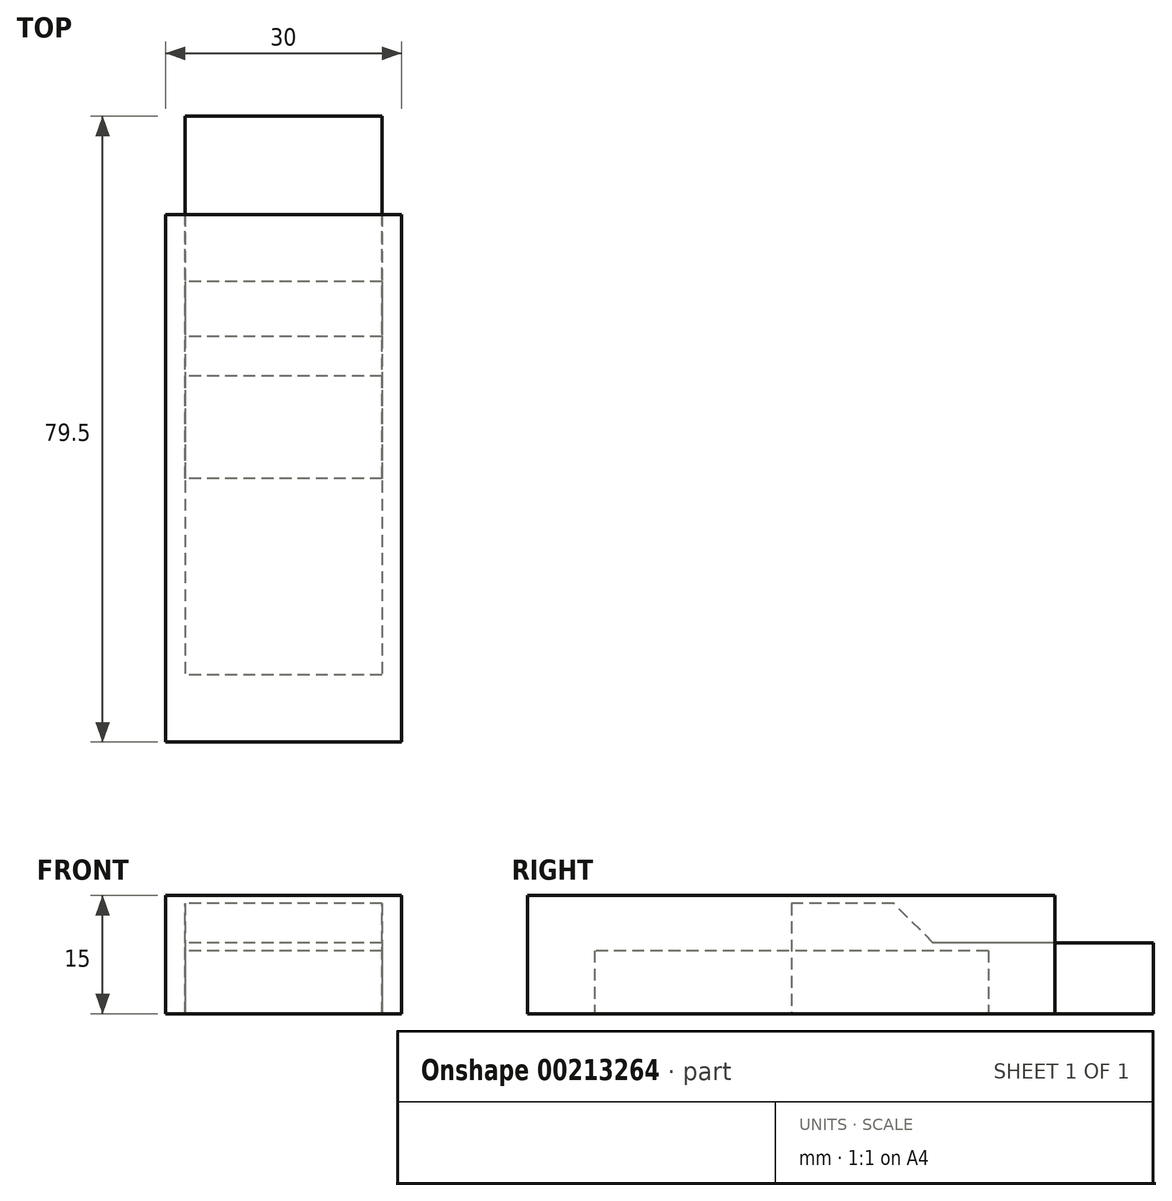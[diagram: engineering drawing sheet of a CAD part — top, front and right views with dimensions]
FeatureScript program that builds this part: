
annotation { "Feature Type Name" : "Feature", "Feature Type Description" : "" }
export const myFeature = defineFeature(function(context is Context, id is Id, definition is map)
    precondition{}
    {
        {
            var Q0;
            Q0=qCreatedBy(makeId("Right.planeOp"),FACE);
            var sketch = newSketch(context, id + "F0", { "sketchPlane" : qUnion([Q0])});
            skLineSegment(sketch, "E0", {"start": v(0, 0) * mm, "end": v(46, 0) * mm});
            skLineSegment(sketch, "E1", {"start": v(46, 0) * mm, "end": v(46, 9) * mm});
            skLineSegment(sketch, "E2", {"start": v(46, 9) * mm, "end": v(18, 9) * mm});
            skLineSegment(sketch, "E3", {"start": v(18, 9) * mm, "end": v(13, 14) * mm});
            skLineSegment(sketch, "E4", {"start": v(13, 14) * mm, "end": v(0, 14) * mm});
            skLineSegment(sketch, "E5", {"start": v(0, 14) * mm, "end": v(0, 0) * mm});
            skSolve(sketch);
        }
        {
            var Q0;
            Q0 = qSketchRegion(id + "F0", true);
            extrude(context, id + "F1", {"entities" : qUnion([Q0]), "depth" : 25 * mm, "symmetric" : true});
        }
        {
            var Q0;
            Q0=qCreatedBy(makeId("Top.planeOp"),FACE);
            var sketch = newSketch(context, id + "F2", { "sketchPlane" : qUnion([Q0])});
            skLineSegment(sketch, "E6.bottom", {"start": v(15, 33.5) * mm, "end": v(-15, 33.5) * mm});
            skLineSegment(sketch, "E6.top", {"start": v(15, -33.5) * mm, "end": v(-15, -33.5) * mm});
            skLineSegment(sketch, "E6.left", {"start": v(15, 33.5) * mm, "end": v(15, -33.5) * mm});
            skLineSegment(sketch, "E6.right", {"start": v(-15, 33.5) * mm, "end": v(-15, -33.5) * mm});
            skPoint(sketch, "E6.middle", {"position": v(0, 0) * mm});
            skSolve(sketch);
        }
        {
            var Q0;
            Q0 = qSketchRegion(id + "F2", true);
            extrude(context, id + "F3", {"entities" : qUnion([Q0]), "depth" : 15 * mm});
        }
        {
            var Q0;
            Q0=qCreatedBy(makeId("Top.planeOp"),FACE);
            var sketch = newSketch(context, id + "F4", { "sketchPlane" : qUnion([Q0])});
            skLineSegment(sketch, "E7.bottom", {"start": v(12.5, 25) * mm, "end": v(-12.5, 25) * mm});
            skLineSegment(sketch, "E7.top", {"start": v(12.5, -25) * mm, "end": v(-12.5, -25) * mm});
            skLineSegment(sketch, "E7.left", {"start": v(12.5, 25) * mm, "end": v(12.5, -25) * mm});
            skLineSegment(sketch, "E7.right", {"start": v(-12.5, 25) * mm, "end": v(-12.5, -25) * mm});
            skPoint(sketch, "E7.middle", {"position": v(0, 0) * mm});
            skSolve(sketch);
        }
        {
            var Q0;
            Q0 = qSketchRegion(id + "F4", true);
            extrude(context, id + "F5", {"entities" : qUnion([Q0]), "depth" : 8 * mm});
        }
    });
